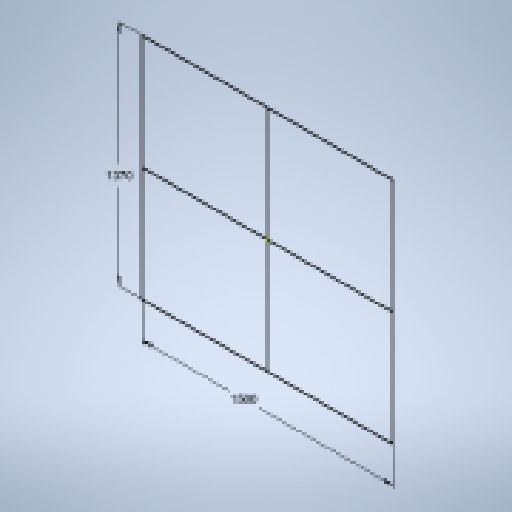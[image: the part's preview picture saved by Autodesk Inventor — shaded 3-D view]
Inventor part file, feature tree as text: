
AUTODESK INVENTOR PART (.ipt)
format: ipt  version: 2025 (Build 290162010, 162A)  size: 129,024 bytes
history: native  units: mm
features: sketch x1
ambient origin geometry x8: Origin, YZ Plane, XZ Plane, XY Plane, X Axis, Y Axis, Z Axis, Center Point
feature tree (1):
  sketch  "Sketch1"  dims[d0=1370.0mm d1=1500.0mm]
